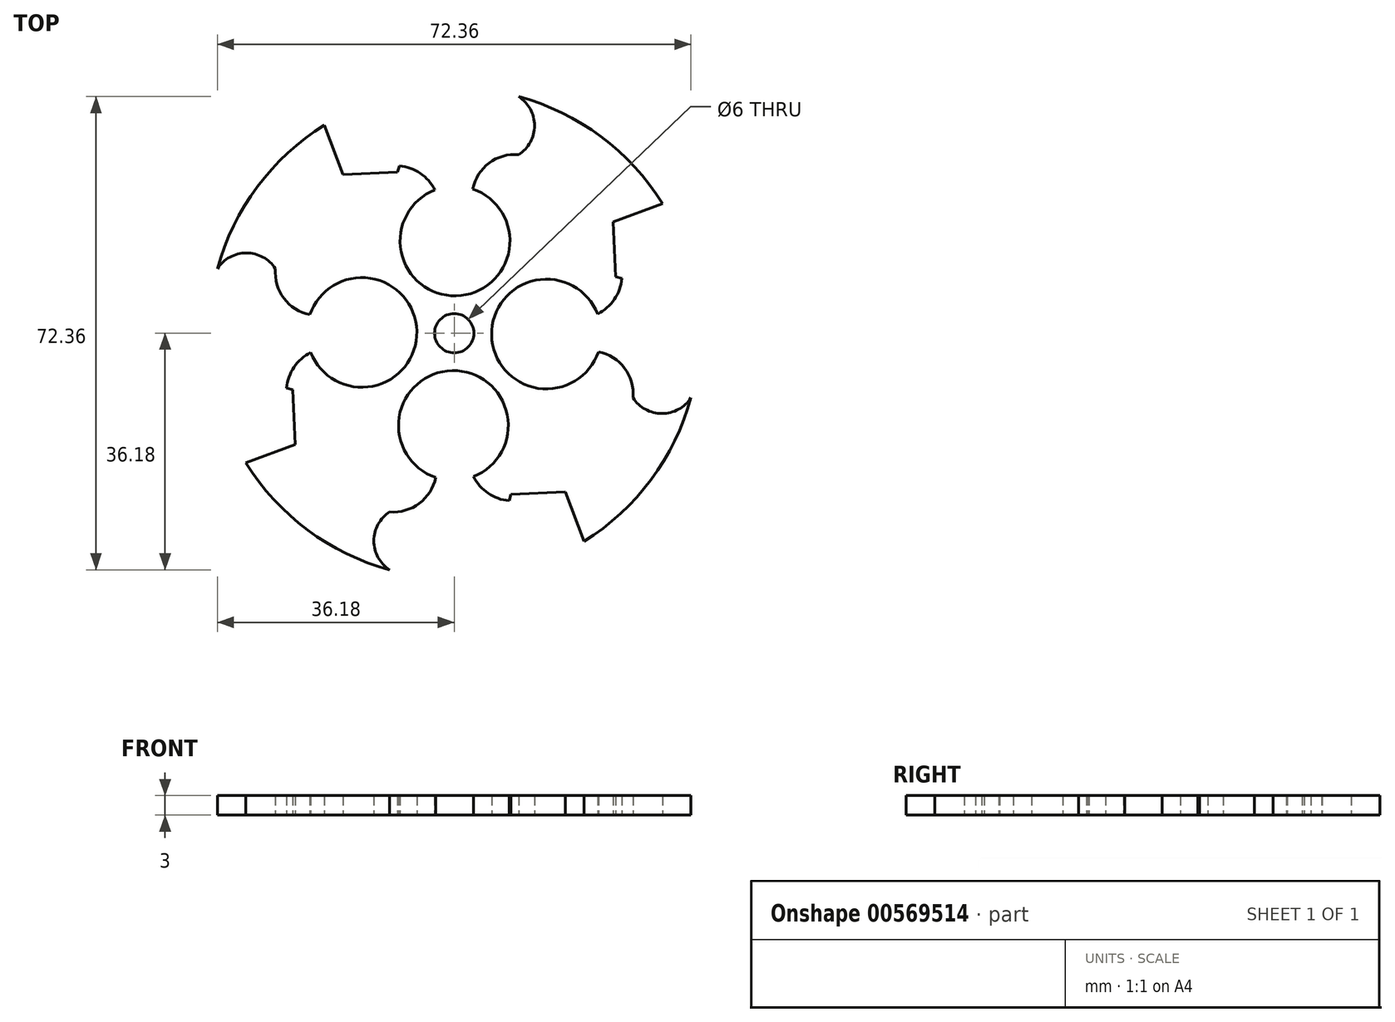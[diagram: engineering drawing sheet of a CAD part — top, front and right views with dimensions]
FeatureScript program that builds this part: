
annotation { "Feature Type Name" : "Feature", "Feature Type Description" : "" }
export const myFeature = defineFeature(function(context is Context, id is Id, definition is map)
    precondition{}
    {
        {
            var Q0;
            Q0=qCreatedBy(makeId("Top.planeOp"),FACE);
            var sketch = newSketch(context, id + "F0", { "sketchPlane" : qUnion([Q0])});
            skLineSegment(sketch, "E0.bottom", {"start": v(0, 0) * mm, "end": v(75, 0) * mm, "construction": true});
            skLineSegment(sketch, "E0.top", {"start": v(0, 75) * mm, "end": v(75, 75) * mm, "construction": true});
            skLineSegment(sketch, "E0.left", {"start": v(0, 0) * mm, "end": v(0, 75) * mm, "construction": true});
            skLineSegment(sketch, "E0.right", {"start": v(75, 0) * mm, "end": v(75, 75) * mm, "construction": true});
            skLineSegment(sketch, "E1", {"start": v(0, 75) * mm, "end": v(75, 0) * mm, "construction": true});
            skCircle(sketch, "E2", {"center": v(37.5, 37.5) * mm, "radius": 37.5 * mm});
            skCircle(sketch, "E3", {"center": v(37.5, 37.5) * mm, "radius": 3 * mm});
            skCircle(sketch, "E4", {"center": v(23.4, 37.62) * mm, "radius": 8.39 * mm});
            skArc(sketch, "E5", {"start": v(25.41, 29.48) * mm, "mid": v(16.2, 34.84) * mm, "end": v(13.03, 24.67) * mm});
            skCircle(sketch, "E6.cCircle", {"center": v(7.28, 24.42) * mm, "radius": 5.76 * mm, "construction": true});
            skLineSegment(sketch, "E6.0", {"start": v(12.85, 28.85) * mm, "end": v(13.22, 20.5) * mm});
            skLineSegment(sketch, "E6.1", {"start": v(13.22, 20.5) * mm, "end": v(5.38, 17.56) * mm});
            skLineSegment(sketch, "E6.2", {"start": v(5.38, 17.56) * mm, "end": v(0.18, 24.1) * mm});
            skLineSegment(sketch, "E6.3", {"start": v(0.18, 24.1) * mm, "end": v(4.8, 31.08) * mm});
            skLineSegment(sketch, "E6.4", {"start": v(4.8, 31.08) * mm, "end": v(12.85, 28.85) * mm});
            skPoint(sketch, "E6.0.midPoint", {"position": v(13.03, 24.67) * mm});
            skArc(sketch, "E7", {"start": v(10.19, 47.36) * mm, "mid": v(16.05, 40.25) * mm, "end": v(23.24, 46.01) * mm});
            skArc(sketch, "E8", {"start": v(10.19, 47.36) * mm, "mid": v(5.75, 49.77) * mm, "end": v(1.32, 47.36) * mm});
            skPoint(sketch, "E9.1.0", {"position": v(50.33, 13.03) * mm});
            skArc(sketch, "E9.1.1", {"start": v(27.64, 10.19) * mm, "mid": v(34.75, 16.05) * mm, "end": v(28.99, 23.24) * mm});
            skCircle(sketch, "E9.1.2", {"center": v(50.58, 7.28) * mm, "radius": 5.76 * mm, "construction": true});
            skArc(sketch, "E9.1.3", {"start": v(45.52, 25.41) * mm, "mid": v(40.16, 16.2) * mm, "end": v(50.33, 13.03) * mm});
            skCircle(sketch, "E9.1.4", {"center": v(37.38, 23.4) * mm, "radius": 8.39 * mm});
            skArc(sketch, "E9.1.5", {"start": v(27.64, 10.19) * mm, "mid": v(25.23, 5.75) * mm, "end": v(27.64, 1.32) * mm});
            skLineSegment(sketch, "E9.1.6", {"start": v(43.92, 4.8) * mm, "end": v(46.15, 12.85) * mm});
            skLineSegment(sketch, "E9.1.7", {"start": v(54.5, 13.22) * mm, "end": v(57.44, 5.38) * mm});
            skLineSegment(sketch, "E9.1.8", {"start": v(50.9, 0.18) * mm, "end": v(43.92, 4.8) * mm});
            skLineSegment(sketch, "E9.1.9", {"start": v(57.44, 5.38) * mm, "end": v(50.9, 0.18) * mm});
            skLineSegment(sketch, "E9.1.10", {"start": v(46.15, 12.85) * mm, "end": v(54.5, 13.22) * mm});
            skPoint(sketch, "E9.2.0", {"position": v(61.97, 50.33) * mm});
            skArc(sketch, "E9.2.1", {"start": v(64.81, 27.64) * mm, "mid": v(58.95, 34.75) * mm, "end": v(51.76, 28.99) * mm});
            skCircle(sketch, "E9.2.2", {"center": v(67.72, 50.58) * mm, "radius": 5.76 * mm, "construction": true});
            skArc(sketch, "E9.2.3", {"start": v(49.59, 45.52) * mm, "mid": v(58.8, 40.16) * mm, "end": v(61.97, 50.33) * mm});
            skCircle(sketch, "E9.2.4", {"center": v(51.6, 37.38) * mm, "radius": 8.39 * mm});
            skArc(sketch, "E9.2.5", {"start": v(64.81, 27.64) * mm, "mid": v(69.25, 25.23) * mm, "end": v(73.68, 27.64) * mm});
            skLineSegment(sketch, "E9.2.6", {"start": v(70.2, 43.92) * mm, "end": v(62.15, 46.15) * mm});
            skLineSegment(sketch, "E9.2.7", {"start": v(61.78, 54.5) * mm, "end": v(69.62, 57.44) * mm});
            skLineSegment(sketch, "E9.2.8", {"start": v(74.82, 50.9) * mm, "end": v(70.2, 43.92) * mm});
            skLineSegment(sketch, "E9.2.9", {"start": v(69.62, 57.44) * mm, "end": v(74.82, 50.9) * mm});
            skLineSegment(sketch, "E9.2.10", {"start": v(62.15, 46.15) * mm, "end": v(61.78, 54.5) * mm});
            skArc(sketch, "E10.1.3.0", {"start": v(47.36, 64.81) * mm, "mid": v(40.25, 58.95) * mm, "end": v(46.01, 51.76) * mm});
            skCircle(sketch, "E10.5.3.0", {"center": v(24.42, 67.72) * mm, "radius": 5.76 * mm, "construction": true});
            skArc(sketch, "E10.7.3.0", {"start": v(29.48, 49.59) * mm, "mid": v(34.84, 58.8) * mm, "end": v(24.67, 61.97) * mm});
            skCircle(sketch, "E10.11.3.0", {"center": v(37.62, 51.6) * mm, "radius": 8.39 * mm});
            skArc(sketch, "E10.13.3.0", {"start": v(47.36, 64.81) * mm, "mid": v(49.77, 69.25) * mm, "end": v(47.36, 73.68) * mm});
            skLineSegment(sketch, "E10.17.3.0", {"start": v(31.08, 70.2) * mm, "end": v(28.85, 62.15) * mm});
            skLineSegment(sketch, "E10.20.3.0", {"start": v(20.5, 61.78) * mm, "end": v(17.56, 69.62) * mm});
            skPoint(sketch, "E10.22.3.0", {"position": v(24.67, 61.97) * mm});
            skLineSegment(sketch, "E10.23.3.0", {"start": v(24.1, 74.82) * mm, "end": v(31.08, 70.2) * mm});
            skLineSegment(sketch, "E10.26.3.0", {"start": v(17.56, 69.62) * mm, "end": v(24.1, 74.82) * mm});
            skLineSegment(sketch, "E10.29.3.0", {"start": v(28.85, 62.15) * mm, "end": v(20.5, 61.78) * mm});
            skSolve(sketch);
        }
        {
            var Q0;
            Q0=makeQuery(id+"F0.imprint","IMPRINT",FACE,{"disambiguationData":[TD([[makeQuery(id+"F0.imprint","IMPRINT",EDGE,{"derivedFrom":sQuery(id+"F0.wireOp",EDGE,"E3")}),-1.0]])]});
            extrude(context, id + "F1", {"entities" : qUnion([Q0]), "depth" : 3 * mm, "offsetDistance" : 25 * mm});
        }
    });
